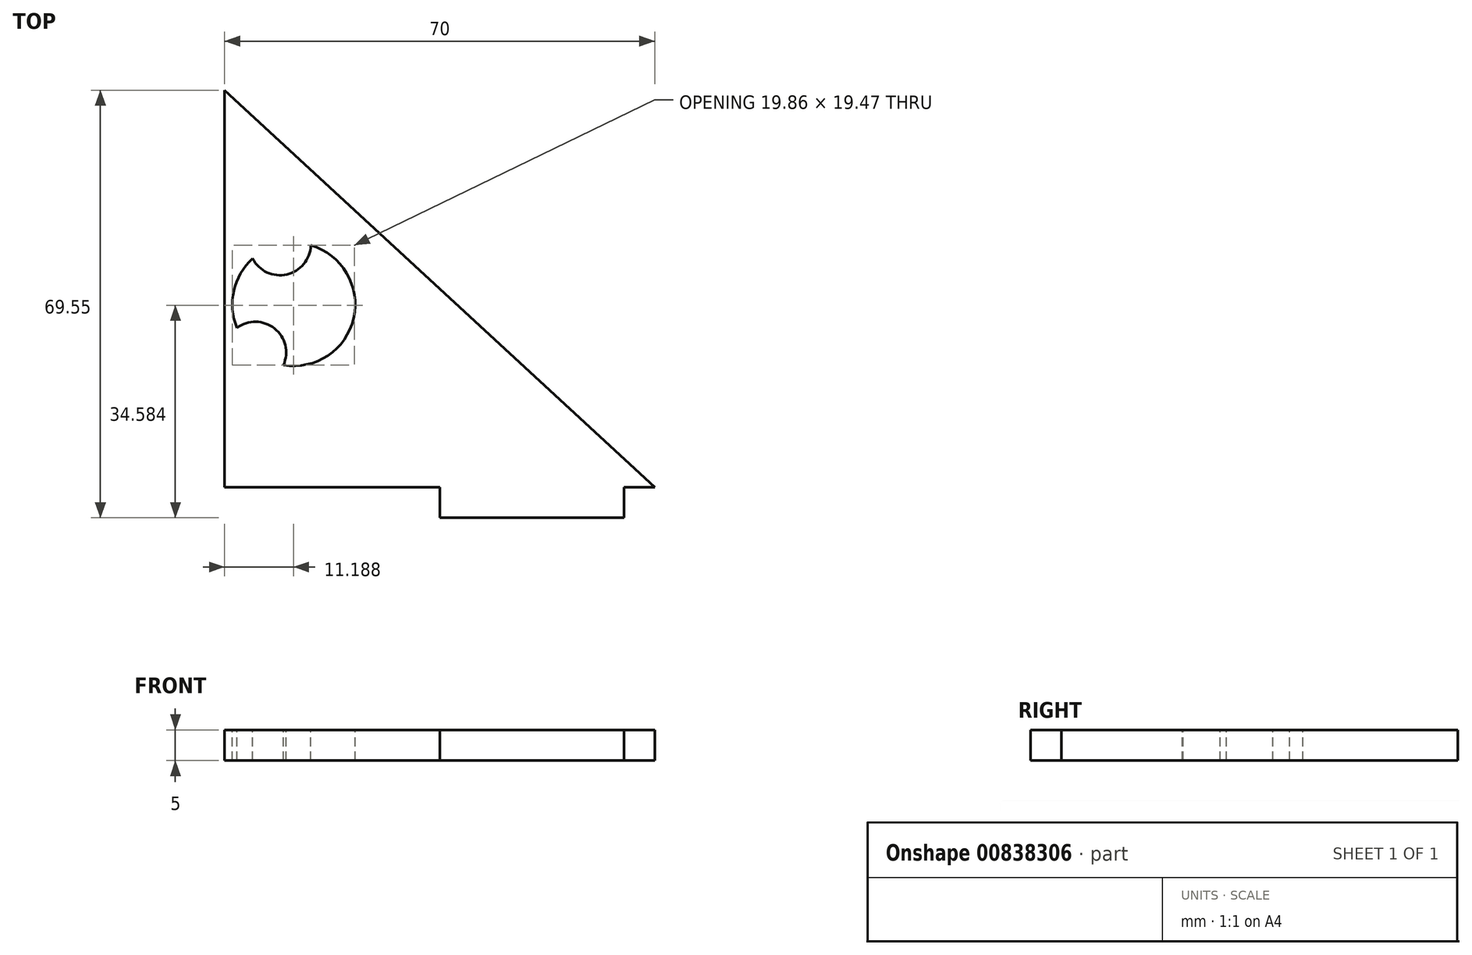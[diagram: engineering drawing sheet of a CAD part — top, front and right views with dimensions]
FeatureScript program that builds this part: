
annotation { "Feature Type Name" : "Feature", "Feature Type Description" : "" }
export const myFeature = defineFeature(function(context is Context, id is Id, definition is map)
    precondition{}
    {
        {
            var Q0;
            Q0=qCreatedBy(makeId("Top.planeOp"),FACE);
            var sketch = newSketch(context, id + "F0", { "sketchPlane" : qUnion([Q0])});
            skLineSegment(sketch, "E0.bottom", {"start": v(35, -80) * mm, "end": v(-35, -80) * mm});
            skLineSegment(sketch, "E0.top", {"start": v(35, 80) * mm, "end": v(-35, 80) * mm});
            skLineSegment(sketch, "E0.left", {"start": v(35, -80) * mm, "end": v(35, 80) * mm});
            skLineSegment(sketch, "E0.right", {"start": v(-35, -80) * mm, "end": v(-35, 80) * mm});
            skPoint(sketch, "E0.middle", {"position": v(0, 0) * mm});
            skLineSegment(sketch, "E1", {"start": v(35, -80) * mm, "end": v(-35, -15.45) * mm});
            skSolve(sketch);
        }
        {
            var Q0;
            {var subQ0=sQuery(id+"F0.wireOp",EDGE,"E0.bottom");Q0=makeQuery(id+"F0.imprint","IMPRINT",FACE,{"disambiguationData":[TD([[makeQuery(id+"F0.imprint","IMPRINT",EDGE,{"derivedFrom":subQ0}),-1.0]])]});}
            extrude(context, id + "F1", {"entities" : qUnion([Q0]), "depth" : 5 * mm, "offsetDistance" : 25 * mm});
        }
        {
            var Q0;
            Q0=makeQuery(id+"F1.opExtrude","CAP_FACE",FACE,{"disambiguationData":[OSD([sQuery(id+"F0.wireOp",EDGE,"E0.bottom"),sQuery(id+"F0.wireOp",EDGE,"E0.right"),sQuery(id+"F0.wireOp",EDGE,"E1")])],"isStart":false});
            var sketch = newSketch(context, id + "F2", { "sketchPlane" : qUnion([Q0])});
            skPoint(sketch, "E2", {"position": v(30, -80) * mm});
            skPoint(sketch, "E3", {"position": v(0, -80) * mm});
            skLineSegment(sketch, "E4.bottom", {"start": v(0, -80) * mm, "end": v(30, -80) * mm});
            skLineSegment(sketch, "E4.top", {"start": v(0, -85) * mm, "end": v(30, -85) * mm});
            skLineSegment(sketch, "E4.left", {"start": v(0, -80) * mm, "end": v(0, -85) * mm});
            skLineSegment(sketch, "E4.right", {"start": v(30, -80) * mm, "end": v(30, -85) * mm});
            skSolve(sketch);
        }
        {
            var Q0;
            Q0 = qSketchRegion(id + "F2", true);
            extrude(context, id + "F3", {"entities" : qUnion([Q0]), "operationType" : NewBodyOperationType.ADD, "oppositeDirection" : true, "depth" : 5 * mm, "offsetDistance" : 25 * mm});
        }
        {
            var Q0;
            Q0=makeQuery(id+"F3.boolean.opBoolean","MERGE",FACE,{"derivedFrom":[makeQuery(id+"F1.opExtrude","CAP_FACE",FACE,{"disambiguationData":[OSD([sQuery(id+"F0.wireOp",EDGE,"E0.bottom"),sQuery(id+"F0.wireOp",EDGE,"E0.right"),sQuery(id+"F0.wireOp",EDGE,"E1")])],"isStart":false}),makeQuery(id+"F3.opExtrude","CAP_FACE",FACE,{"disambiguationData":[OSD([sQuery(id+"F2.wireOp",EDGE,"E4.bottom"),sQuery(id+"F2.wireOp",EDGE,"E4.top"),sQuery(id+"F2.wireOp",EDGE,"E4.left"),sQuery(id+"F2.wireOp",EDGE,"E4.right")])],"isStart":true})]});
            var sketch = newSketch(context, id + "F4", { "sketchPlane" : qUnion([Q0])});
            skPoint(sketch, "E5", {"position": v(-35, -47.73) * mm});
            skCircle(sketch, "E6.cCircle", {"center": v(-35, -47.73) * mm, "radius": 10.38 * mm, "construction": true});
            skLineSegment(sketch, "E6.0", {"start": v(-23.77, -50.29) * mm, "end": v(-30, -58.1) * mm});
            skLineSegment(sketch, "E6.1", {"start": v(-30, -58.1) * mm, "end": v(-40, -58.1) * mm});
            skLineSegment(sketch, "E6.2", {"start": v(-40, -58.1) * mm, "end": v(-46.23, -50.29) * mm});
            skLineSegment(sketch, "E6.3", {"start": v(-46.23, -50.29) * mm, "end": v(-44, -40.54) * mm});
            skLineSegment(sketch, "E6.4", {"start": v(-44, -40.54) * mm, "end": v(-35, -36.2) * mm});
            skLineSegment(sketch, "E6.5", {"start": v(-35, -36.2) * mm, "end": v(-26, -40.54) * mm});
            skLineSegment(sketch, "E6.6", {"start": v(-26, -40.54) * mm, "end": v(-23.77, -50.29) * mm});
            skPoint(sketch, "E6.0.midPoint", {"position": v(-26.88, -54.2) * mm});
            skCircle(sketch, "E7", {"center": v(-35, -36.2) * mm, "radius": 5 * mm});
            skCircle(sketch, "E8", {"center": v(-26, -40.54) * mm, "radius": 5 * mm});
            skCircle(sketch, "E9", {"center": v(-23.77, -50.29) * mm, "radius": 10 * mm});
            skCircle(sketch, "E10", {"center": v(-30, -58.1) * mm, "radius": 5 * mm});
            skSolve(sketch);
        }
        {
            var Q0;
            {var subQ1=sQuery(id+"F4.wireOp",EDGE,"E6.6");var subQ6=sQuery(id+"F4.wireOp",EDGE,"E6.0");var subQ9=makeQuery(id+"F4.imprint","INTERSECT",VERTEX,{"derivedFrom":[subQ6,subQ1]});Q0=makeQuery(id+"F4.imprint","IMPRINT",FACE,{"disambiguationData":[TD([[makeQuery(id+"F4.imprint","IMPRINT",EDGE,{"disambiguationData":[TD([[subQ9,-1.0]])],"derivedFrom":subQ6}),1.0]])]});}
            var Q1;
            {var subQ5=sQuery(id+"F4.wireOp",EDGE,"E6.6");var subQ6=sQuery(id+"F4.wireOp",EDGE,"E6.0");var subQ7=makeQuery(id+"F4.imprint","INTERSECT",VERTEX,{"derivedFrom":[subQ6,subQ5]});Q1=makeQuery(id+"F4.imprint","IMPRINT",FACE,{"disambiguationData":[TD([[makeQuery(id+"F4.imprint","IMPRINT",EDGE,{"disambiguationData":[TD([[subQ7,-1.0]])],"derivedFrom":subQ6}),-1.0]])]});}
            extrude(context, id + "F5", {"entities" : qUnion([Q0, Q1]), "operationType" : NewBodyOperationType.REMOVE, "endBound" : BoundingType.THROUGH_ALL, "oppositeDirection" : true, "depth" : 25 * mm, "offsetDistance" : 25 * mm});
        }
    });
